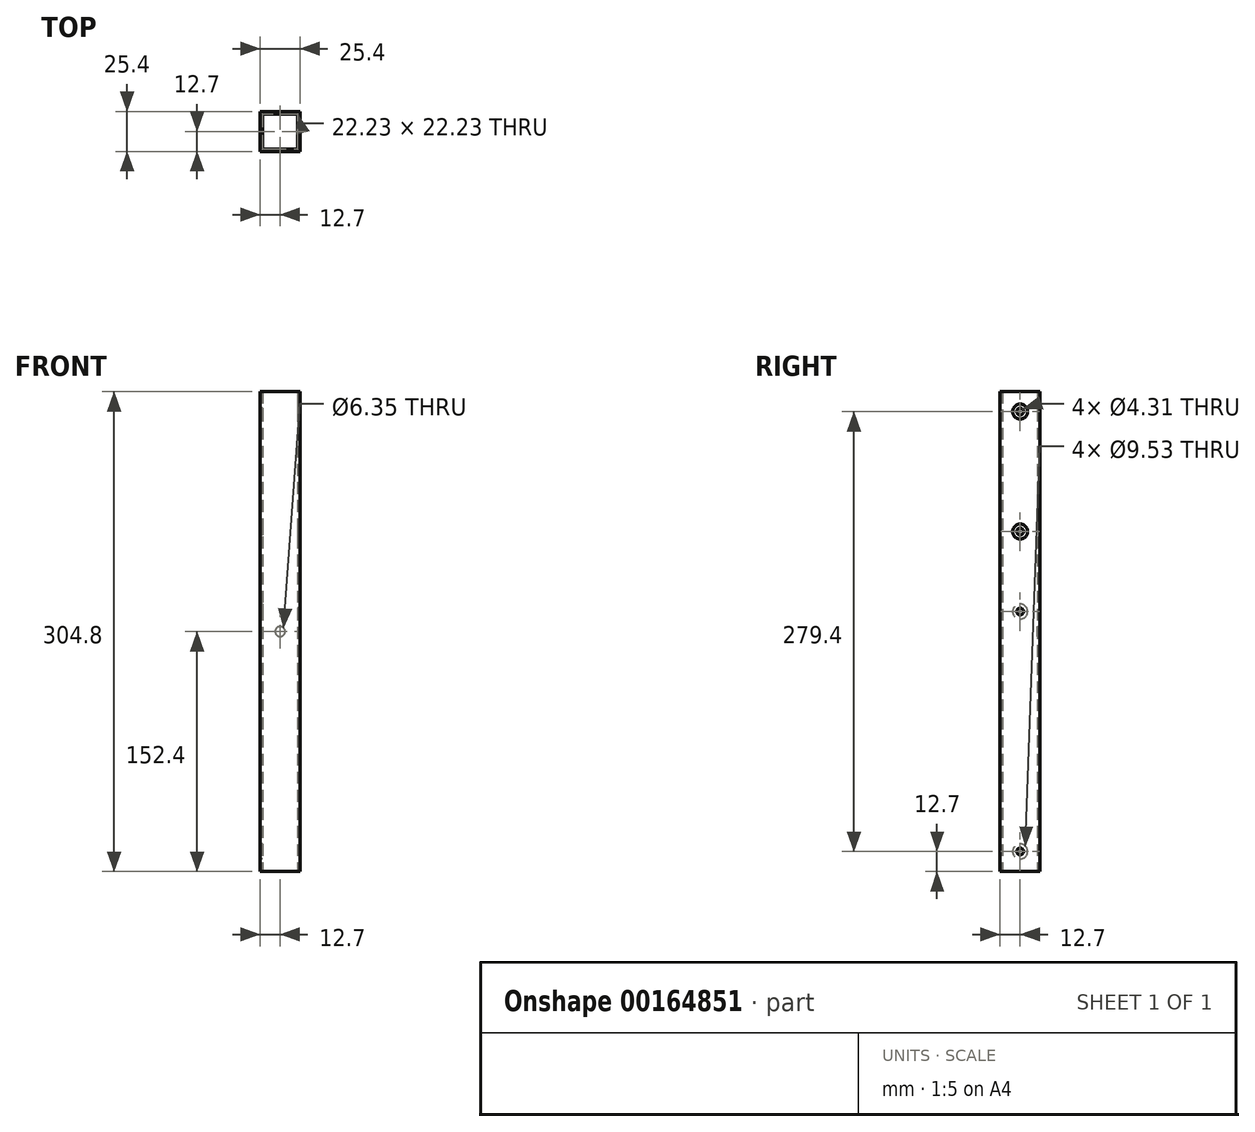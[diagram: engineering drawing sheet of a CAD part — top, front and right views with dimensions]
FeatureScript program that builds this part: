
annotation { "Feature Type Name" : "Feature", "Feature Type Description" : "" }
export const myFeature = defineFeature(function(context is Context, id is Id, definition is map)
    precondition{}
    {
        {
            var Q0;
            Q0=qCreatedBy(makeId("Top.planeOp"),FACE);
            var sketch = newSketch(context, id + "F0", { "sketchPlane" : qUnion([Q0])});
            skLineSegment(sketch, "E0.bottom", {"start": v(11.11, -11.11) * mm, "end": v(-11.11, -11.11) * mm});
            skLineSegment(sketch, "E0.top", {"start": v(11.11, 11.11) * mm, "end": v(-11.11, 11.11) * mm});
            skLineSegment(sketch, "E0.left", {"start": v(11.11, -11.11) * mm, "end": v(11.11, 11.11) * mm});
            skLineSegment(sketch, "E0.right", {"start": v(-11.11, -11.11) * mm, "end": v(-11.11, 11.11) * mm});
            skPoint(sketch, "E0.middle", {"position": v(0, 0) * mm});
            skLineSegment(sketch, "E1.bottom", {"start": v(12.7, -12.7) * mm, "end": v(-12.7, -12.7) * mm});
            skLineSegment(sketch, "E1.top", {"start": v(12.7, 12.7) * mm, "end": v(-12.7, 12.7) * mm});
            skLineSegment(sketch, "E1.left", {"start": v(12.7, -12.7) * mm, "end": v(12.7, 12.7) * mm});
            skLineSegment(sketch, "E1.right", {"start": v(-12.7, -12.7) * mm, "end": v(-12.7, 12.7) * mm});
            skSolve(sketch);
        }
        {
            var Q0;
            Q0=qSketchRegion(id+"F0",true);
            extrude(context, id + "F1", {"entities" : qUnion([Q0]), "depth" : 304.8 * mm});
        }
        {
            var Q0;
            Q0=makeQuery(id+"F1.opExtrude","SWEPT_FACE",FACE,{"disambiguationData":[OSD([sQuery(id+"F0.wireOp",EDGE,"E1.top")])]});
            var sketch = newSketch(context, id + "F2", { "sketchPlane" : qUnion([Q0])});
            skLineSegment(sketch, "E2", {"start": v(12.7, 152.4) * mm, "end": v(-12.7, 152.4) * mm, "construction": true});
            skCircle(sketch, "E3", {"center": v(0, 152.4) * mm, "radius": 3.17 * mm});
            skSolve(sketch);
        }
        {
            var Q0;
            Q0=qSketchRegion(id+"F2",true);
            var Q1;
            Q1=makeQuery(id+"F1.opExtrude","SWEPT_FACE",FACE,{"disambiguationData":[OSD([sQuery(id+"F0.wireOp",EDGE,"E0.top")])]});
            extrude(context, id + "F3", {"entities" : qUnion([Q0]), "operationType" : NewBodyOperationType.REMOVE, "endBound" : BoundingType.UP_TO_SURFACE, "oppositeDirection" : true, "endBoundEntityFace" : qUnion([Q1]), "depth" : 25.4 * mm});
        }
        {
            var Q0;
            Q0=makeQuery(id+"F1.opExtrude","SWEPT_FACE",FACE,{"disambiguationData":[OSD([sQuery(id+"F0.wireOp",EDGE,"E1.right")])]});
            var sketch = newSketch(context, id + "F4", { "sketchPlane" : qUnion([Q0])});
            skLineSegment(sketch, "E4.bottom", {"start": v(0, 0) * mm, "end": v(-12.7, 0) * mm, "construction": true});
            skLineSegment(sketch, "E4.top", {"start": v(0, 12.7) * mm, "end": v(-12.7, 12.7) * mm, "construction": true});
            skLineSegment(sketch, "E4.left", {"start": v(0, 0) * mm, "end": v(0, 12.7) * mm, "construction": true});
            skLineSegment(sketch, "E4.right", {"start": v(-12.7, 0) * mm, "end": v(-12.7, 12.7) * mm, "construction": true});
            skLineSegment(sketch, "E5.bottom", {"start": v(0, 304.8) * mm, "end": v(-12.7, 304.8) * mm, "construction": true});
            skLineSegment(sketch, "E5.top", {"start": v(0, 292.1) * mm, "end": v(-12.7, 292.1) * mm, "construction": true});
            skLineSegment(sketch, "E5.left", {"start": v(0, 304.8) * mm, "end": v(0, 292.1) * mm, "construction": true});
            skLineSegment(sketch, "E5.right", {"start": v(-12.7, 304.8) * mm, "end": v(-12.7, 292.1) * mm, "construction": true});
            skLineSegment(sketch, "E6", {"start": v(0, 12.7) * mm, "end": v(0, 165.1) * mm, "construction": true});
            skLineSegment(sketch, "E7", {"start": v(0, 292.1) * mm, "end": v(0, 215.9) * mm, "construction": true});
            skCircle(sketch, "E8", {"center": v(0, 12.7) * mm, "radius": 2.15 * mm});
            skCircle(sketch, "E9", {"center": v(0, 165.1) * mm, "radius": 2.15 * mm});
            skCircle(sketch, "E10", {"center": v(0, 292.1) * mm, "radius": 2.15 * mm});
            skCircle(sketch, "E11", {"center": v(0, 215.9) * mm, "radius": 2.15 * mm});
            skSolve(sketch);
        }
        {
            var Q0;
            Q0=qSketchRegion(id+"F4",true);
            var Q1;
            Q1=makeQuery(id+"F1.opExtrude","SWEPT_FACE",FACE,{"disambiguationData":[OSD([sQuery(id+"F0.wireOp",EDGE,"E1.left")])]});
            extrude(context, id + "F5", {"entities" : qUnion([Q0]), "operationType" : NewBodyOperationType.REMOVE, "endBound" : BoundingType.UP_TO_SURFACE, "oppositeDirection" : true, "endBoundEntityFace" : qUnion([Q1]), "depth" : 25.4 * mm});
        }
        {
            var Q0;
            Q0=makeQuery(id+"F1.opExtrude","SWEPT_FACE",FACE,{"disambiguationData":[OSD([sQuery(id+"F0.wireOp",EDGE,"E1.left")])]});
            var sketch = newSketch(context, id + "F6", { "sketchPlane" : qUnion([Q0])});
            skCircle(sketch, "E12", {"center": v(0, 292.1) * mm, "radius": 4.76 * mm});
            skCircle(sketch, "E13", {"center": v(0, 215.9) * mm, "radius": 4.76 * mm});
            skSolve(sketch);
        }
        {
            var Q0;
            Q0=qSketchRegion(id+"F6",true);
            var Q1;
            Q1=makeQuery(id+"F1.opExtrude","SWEPT_FACE",FACE,{"disambiguationData":[OSD([sQuery(id+"F0.wireOp",EDGE,"E0.left")])]});
            extrude(context, id + "F7", {"entities" : qUnion([Q0]), "operationType" : NewBodyOperationType.REMOVE, "endBound" : BoundingType.UP_TO_SURFACE, "oppositeDirection" : true, "endBoundEntityFace" : qUnion([Q1]), "depth" : 25.4 * mm});
        }
        {
            var Q0;
            Q0=makeQuery(id+"F1.opExtrude","SWEPT_FACE",FACE,{"disambiguationData":[OSD([sQuery(id+"F0.wireOp",EDGE,"E1.right")])]});
            var sketch = newSketch(context, id + "F8", { "sketchPlane" : qUnion([Q0])});
            skCircle(sketch, "E14", {"center": v(0, 165.1) * mm, "radius": 4.76 * mm});
            skCircle(sketch, "E15", {"center": v(0, 12.7) * mm, "radius": 4.76 * mm});
            skSolve(sketch);
        }
        {
            var Q0;
            Q0=qSketchRegion(id+"F8",true);
            var Q1;
            Q1=makeQuery(id+"F1.opExtrude","SWEPT_FACE",FACE,{"disambiguationData":[OSD([sQuery(id+"F0.wireOp",EDGE,"E0.right")])]});
            extrude(context, id + "F9", {"entities" : qUnion([Q0]), "operationType" : NewBodyOperationType.REMOVE, "endBound" : BoundingType.UP_TO_SURFACE, "oppositeDirection" : true, "endBoundEntityFace" : qUnion([Q1]), "depth" : 25.4 * mm});
        }
    });
